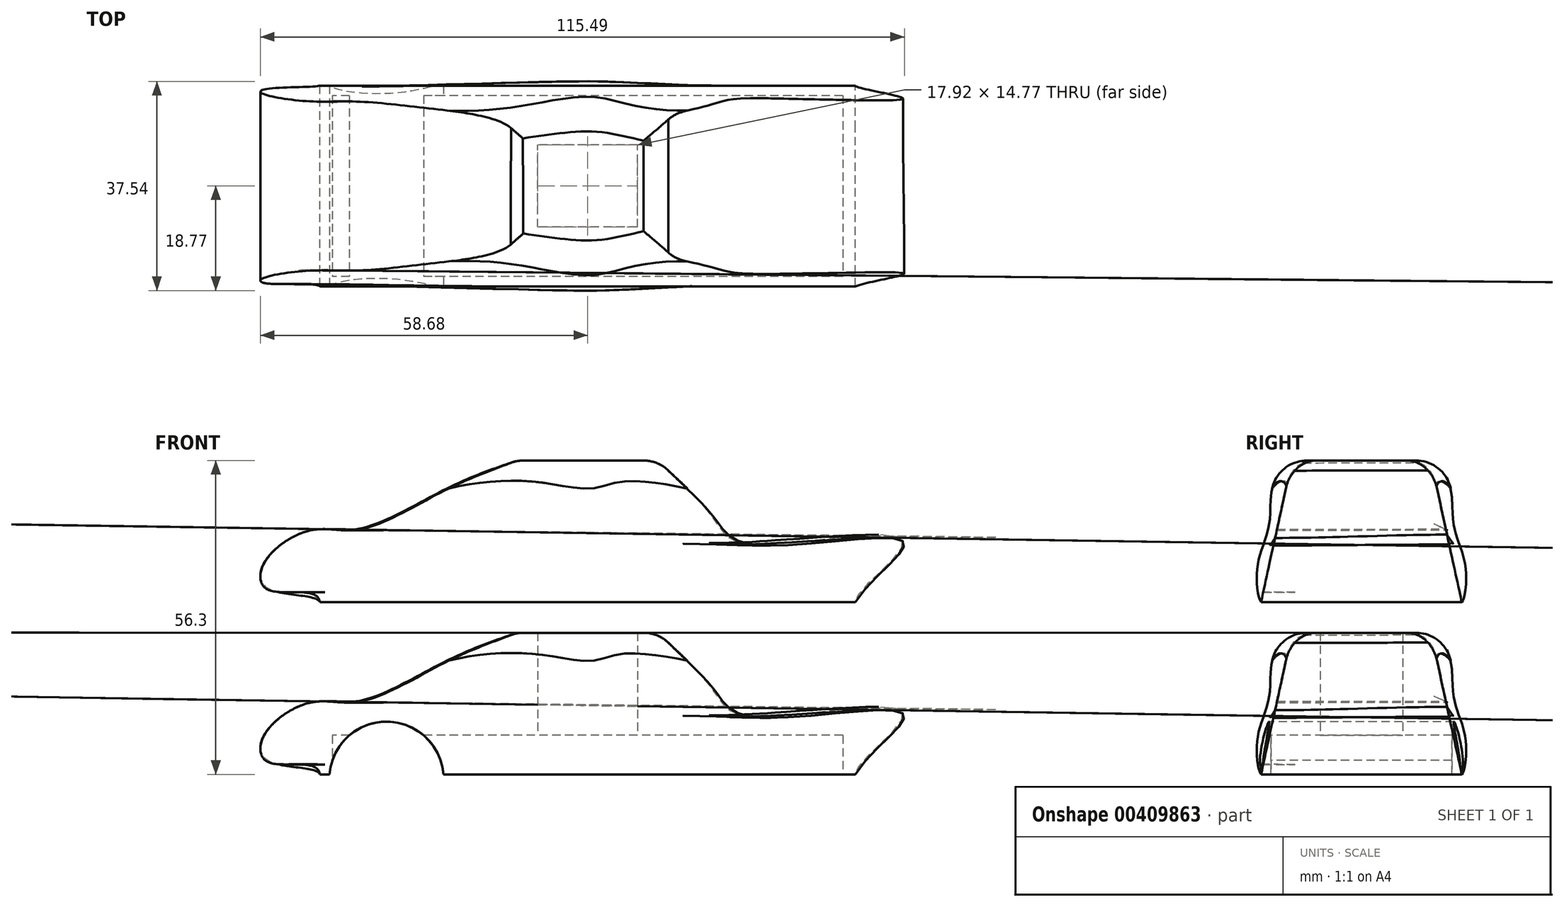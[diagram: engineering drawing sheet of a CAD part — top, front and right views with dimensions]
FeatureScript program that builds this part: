
annotation { "Feature Type Name" : "Feature", "Feature Type Description" : "" }
export const myFeature = defineFeature(function(context is Context, id is Id, definition is map)
    precondition{}
    {
        {
            var Q0;
            Q0=qCreatedBy(makeId("Top.planeOp"),FACE);
            var sketch = newSketch(context, id + "F0", { "sketchPlane" : qUnion([Q0])});
            skLineSegment(sketch, "E0.bottom", {"start": v(48, -18) * mm, "end": v(-48, -18) * mm});
            skLineSegment(sketch, "E0.top", {"start": v(48, 18) * mm, "end": v(-48, 18) * mm});
            skLineSegment(sketch, "E0.left", {"start": v(48, -18) * mm, "end": v(48, 18) * mm});
            skLineSegment(sketch, "E0.right", {"start": v(-48, -18) * mm, "end": v(-48, 18) * mm});
            skPoint(sketch, "E0.middle", {"position": v(0, 0) * mm});
            skLineSegment(sketch, "E1", {"start": v(0, 18) * mm, "end": v(0, -18) * mm, "construction": true});
            skSolve(sketch);
        }
        {
            var Q0;
            Q0=sQuery(id+"F0.wireOp",EDGE,"E0.bottom");
            cPoint(context, id + "F1", {"entities" : qUnion([Q0]), "parameter" : 0.5});
        }
        {
            var Q0;
            Q0=sQuery(id+"F0.wireOp",EDGE,"E1");
            var Q1;
            Q1 = qCreatedBy(id + "F1" ,VERTEX);
            cPlane(context, id + "F2", {"entities" : qUnion([Q0, Q1]), "cplaneType" : CPlaneType.LINE_POINT, "offset" : 25.4 * mm, "width" : 152.4 * mm, "height" : 152.4 * mm});
        }
        {
            var Q0;
            Q0=qCreatedBy(makeId("Top.planeOp"),FACE);
            cPlane(context, id + "F3", {"entities" : qUnion([Q0]), "cplaneType" : CPlaneType.OFFSET, "offset" : 25.4 * mm, "width" : 152.4 * mm, "height" : 152.4 * mm});
        }
        {
            var Q0;
            Q0=qCreatedBy(id+"F3.planeOp",FACE);
            var sketch = newSketch(context, id + "F4", { "sketchPlane" : qUnion([Q0])});
            skLineSegment(sketch, "E2.bottom", {"start": v(12.7, -12.45) * mm, "end": v(-12.7, -12.45) * mm});
            skLineSegment(sketch, "E2.top", {"start": v(12.7, 12.45) * mm, "end": v(-12.7, 12.45) * mm});
            skLineSegment(sketch, "E2.left", {"start": v(12.7, -12.45) * mm, "end": v(12.7, 12.45) * mm});
            skLineSegment(sketch, "E2.right", {"start": v(-12.7, -12.45) * mm, "end": v(-12.7, 12.45) * mm});
            skPoint(sketch, "E2.middle", {"position": v(0, 0) * mm});
            skLineSegment(sketch, "E3", {"start": v(0, 0) * mm, "end": v(0, -12.45) * mm, "construction": true});
            skLineSegment(sketch, "E4", {"start": v(-12.7, 0) * mm, "end": v(12.7, 0) * mm, "construction": true});
            skLineSegment(sketch, "E5", {"start": v(0, 0) * mm, "end": v(0, 12.45) * mm, "construction": true});
            skSolve(sketch);
        }
        {
            var Q0;
            Q0=sQuery(id+"F4.wireOp",VERTEX,"E3.end");
            var Q1;
            Q1=sQuery(id+"F0.wireOp",VERTEX,"E0.right.start");
            var Q2;
            Q2=sQuery(id+"F0.wireOp",VERTEX,"E0.bottom.start");
            cPlane(context, id + "F5", {"entities" : qUnion([Q0, Q1, Q2]), "cplaneType" : CPlaneType.THREE_POINT, "offset" : 25.4 * mm, "width" : 152.4 * mm, "height" : 152.4 * mm});
        }
        {
            var Q0;
            Q0=qCreatedBy(id+"F5.planeOp",FACE);
            var sketch = newSketch(context, id + "F6", { "sketchPlane" : qUnion([Q0])});
            skFitSpline(sketch, "E6", {"points": [v(12.7, 22.16) * mm, v(25.28, 16.84) * mm, v(40.86, 9.52) * mm, v(49.57, 9.36) * mm, v(58.12, 3.05) * mm, v(56.98, -1.7) * mm, v(48, -3.84) * mm], "startDerivative": vector(60.22, -24.2) * mm, "endDerivative": vector(-7.7, -56.28) * mm});
            skFitSpline(sketch, "E7", {"points": [v(-12.7, 22.16) * mm, v(-19.43, 15.4) * mm, v(-23.32, 10.85) * mm, v(-29.51, 6.74) * mm, v(-56.65, 7.22) * mm, v(-48, -3.84) * mm], "startDerivative": vector(-31.26, -33.19) * mm, "endDerivative": vector(39.78, -64.87) * mm});
            skSolve(sketch);
        }
        {
            var Q0;
            Q0=sQuery(id+"F4.wireOp",EDGE,"E2.top");
            cPoint(context, id + "F7", {"entities" : qUnion([Q0]), "parameter" : 0.5});
        }
        {
            var Q0;
            Q0 = qCreatedBy(id + "F7" ,VERTEX);
            var Q1;
            Q1=sQuery(id+"F0.wireOp",VERTEX,"E0.left.end");
            var Q2;
            Q2=sQuery(id+"F0.wireOp",VERTEX,"E0.right.end");
            cPlane(context, id + "F8", {"entities" : qUnion([Q0, Q1, Q2]), "cplaneType" : CPlaneType.THREE_POINT, "offset" : 25.4 * mm, "width" : 152.4 * mm, "height" : 152.4 * mm});
        }
        {
            var Q0;
            Q0=qCreatedBy(id+"F8.planeOp",FACE);
            var sketch = newSketch(context, id + "F9", { "sketchPlane" : qUnion([Q0])});
            skFitSpline(sketch, "E8", {"points": [v(12.7, 22.16) * mm, v(19.29, 15.59) * mm, v(23.6, 10) * mm, v(29.61, 6.76) * mm, v(56.55, 7.19) * mm, v(48, -3.84) * mm], "startDerivative": vector(33.12, -36.07) * mm, "endDerivative": vector(5.37, -27.82) * mm});
            skFitSpline(sketch, "E9", {"points": [v(-12.45, 22.25) * mm, v(-24.96, 17.16) * mm, v(-41.15, 9.6) * mm, v(-49.8, 9.32) * mm, v(-58.17, 3.06) * mm, v(-56.92, -1.5) * mm, v(-48, -3.84) * mm], "startDerivative": vector(-64.64, -23.54) * mm, "endDerivative": vector(9.88, -27.36) * mm});
            skSolve(sketch);
        }
        {
            var Q0;
            Q0=sQuery(id+"F0.wireOp",EDGE,"E0.bottom");
            cPlane(context, id + "F10", {"entities" : qUnion([Q0]), "cplaneType" : CPlaneType.MID_PLANE, "offset" : 25.4 * mm, "width" : 152.4 * mm, "height" : 152.4 * mm});
        }
        {
            var Q0;
            Q0=qCreatedBy(id+"F10.planeOp",FACE);
            var sketch = newSketch(context, id + "F11", { "sketchPlane" : qUnion([Q0])});
            skFitSpline(sketch, "E10", {"points": [v(12.45, 25.4) * mm, v(16.46, 14.53) * mm, v(18.6, 6.63) * mm, v(18, 0) * mm], "startDerivative": vector(36.42, -22.65) * mm, "endDerivative": vector(-6.58, -9) * mm});
            skLineSegment(sketch, "E11", {"start": v(0, 25.4) * mm, "end": v(0, 0) * mm, "construction": true});
            skFitSpline(sketch, "E12.MirrorCS", {"points": [v(-12.45, 25.4) * mm, v(-16.46, 14.53) * mm, v(-18.6, 6.63) * mm, v(-18, 0) * mm], "startDerivative": vector(-36.42, -22.65) * mm, "endDerivative": vector(6.58, -9) * mm});
            skSolve(sketch);
        }
        {
            var Q0;
            Q0=makeQuery(id+"F0.imprint","IMPRINT",FACE,{"disambiguationData":[TD([[makeQuery(id+"F0.imprint","IMPRINT",EDGE,{"derivedFrom":sQuery(id+"F0.wireOp",EDGE,"E0.bottom")}),-1.0]])]});
            var Q1;
            Q1=makeQuery(id+"F4.imprint","IMPRINT",FACE,{"disambiguationData":[TD([[makeQuery(id+"F4.imprint","IMPRINT",EDGE,{"derivedFrom":sQuery(id+"F4.wireOp",EDGE,"E2.bottom")}),-1.0]])]});
            var Q2;
            Q2=sQuery(id+"F9.wireOp",EDGE,"E9");
            var Q3;
            Q3=sQuery(id+"F6.wireOp",EDGE,"E6");
            var Q4;
            Q4=sQuery(id+"F6.wireOp",EDGE,"E7");
            var Q5;
            Q5=sQuery(id+"F9.wireOp",EDGE,"E8");
            var Q6;
            Q6=sQuery(id+"F11.wireOp",EDGE,"E12.MirrorCS");
            var Q7;
            Q7=sQuery(id+"F11.wireOp",EDGE,"E10");
            loft(context, id + "F12", {"addGuides" : true, "sheetProfilesArray" : [{ "sheetProfileEntities" : qUnion([Q0]) }, { "sheetProfileEntities" : qUnion([Q1]) }], "guidesArray" : [{ "guideEntities" : qUnion([Q2]), "guideDerivativeType" : LoftGuideDerivativeType.DEFAULT, "guideDerivativeMagnitude" : 1 }, { "guideEntities" : qUnion([Q3]), "guideDerivativeType" : LoftGuideDerivativeType.DEFAULT, "guideDerivativeMagnitude" : 1 }, { "guideEntities" : qUnion([Q4]), "guideDerivativeType" : LoftGuideDerivativeType.DEFAULT, "guideDerivativeMagnitude" : 1 }, { "guideEntities" : qUnion([Q5]), "guideDerivativeType" : LoftGuideDerivativeType.DEFAULT, "guideDerivativeMagnitude" : 1 }, { "guideEntities" : qUnion([Q6]), "guideDerivativeType" : LoftGuideDerivativeType.DEFAULT, "guideDerivativeMagnitude" : 1 }, { "guideEntities" : qUnion([Q7]), "guideDerivativeType" : LoftGuideDerivativeType.DEFAULT, "guideDerivativeMagnitude" : 1 }]});
        }
        {
            var Q0;
            Q0=makeQuery(id+"F12.opLoft","MID_CAP_EDGE",EDGE,{"disambiguationData":[OSD([sQuery(id+"F4.wireOp",EDGE,"E2.right"),sQuery(id+"F6.wireOp",EDGE,"E6"),sQuery(id+"F9.wireOp",EDGE,"E9")])],"capPos":1.0});
            var Q1;
            Q1=makeQuery(id+"F12.opLoft","MID_CAP_EDGE",EDGE,{"disambiguationData":[OSD([sQuery(id+"F4.wireOp",EDGE,"E2.bottom"),sQuery(id+"F6.wireOp",EDGE,"E6"),sQuery(id+"F11.wireOp",EDGE,"E10")])],"capPos":1.0});
            var Q2;
            Q2=makeQuery(id+"F12.opLoft","MID_CAP_EDGE",EDGE,{"disambiguationData":[OSD([sQuery(id+"F4.wireOp",EDGE,"E2.top"),sQuery(id+"F9.wireOp",EDGE,"E8"),sQuery(id+"F11.wireOp",EDGE,"E12.MirrorCS")])],"capPos":1.0});
            var Q3;
            Q3=makeQuery(id+"F12.opLoft","MID_CAP_EDGE",EDGE,{"disambiguationData":[OSD([sQuery(id+"F4.wireOp",EDGE,"E2.left"),sQuery(id+"F6.wireOp",EDGE,"E7"),sQuery(id+"F9.wireOp",EDGE,"E8")])],"capPos":1.0});
            fillet(context, id + "F13", {"entities" : qUnion([Q0, Q1, Q2, Q3]), "radius" : 6.35 * mm, "allowEdgeOverflow" : false});
        }
        {
            var Q0;
            Q0=makeQuery(id+"F12.opLoft","SWEPT_BODY",BODY,{"disambiguationData":[OSD([makeQuery(id+"F0.imprint","IMPRINT",FACE,{"disambiguationData":[TD([[makeQuery(id+"F0.imprint","IMPRINT",EDGE,{"derivedFrom":sQuery(id+"F0.wireOp",EDGE,"E0.bottom")}),-1.0]])]}),makeQuery(id+"F4.imprint","IMPRINT",FACE,{"disambiguationData":[TD([[makeQuery(id+"F4.imprint","IMPRINT",EDGE,{"derivedFrom":sQuery(id+"F4.wireOp",EDGE,"E2.bottom")}),-1.0]])]}),sQuery(id+"F6.wireOp",EDGE,"E6"),sQuery(id+"F6.wireOp",EDGE,"E7"),sQuery(id+"F9.wireOp",EDGE,"E8"),sQuery(id+"F9.wireOp",EDGE,"E9"),sQuery(id+"F11.wireOp",EDGE,"E10"),sQuery(id+"F11.wireOp",EDGE,"E12.MirrorCS")])]});
            transform(context, id + "F14", {"entities" : qUnion([Q0]), "transformType" : TransformType.TRANSLATION_3D, "dx" : 0 * mm, "dy" : 0 * mm, "dz" : -30.9 * mm, "makeCopy" : true});
        }
        {
            var Q0;
            Q0=makeQuery(id+"F14.opPattern","COPY",FACE,{"derivedFrom":makeQuery(id+"F12.opLoft","CAP_FACE",FACE,{"disambiguationData":[OSD([makeQuery(id+"F0.imprint","IMPRINT",FACE,{"disambiguationData":[TD([[makeQuery(id+"F0.imprint","IMPRINT",EDGE,{"derivedFrom":sQuery(id+"F0.wireOp",EDGE,"E0.bottom")}),-1.0]])]})])],"isStart":true}),"instanceName":"1"});
            var sketch = newSketch(context, id + "F15", { "sketchPlane" : qUnion([Q0])});
            skLineSegment(sketch, "E13.bottom", {"start": v(45.76, -16.22) * mm, "end": v(-45.76, -16.22) * mm});
            skLineSegment(sketch, "E13.top", {"start": v(45.76, 16.22) * mm, "end": v(-45.76, 16.22) * mm});
            skLineSegment(sketch, "E13.left", {"start": v(45.76, -16.22) * mm, "end": v(45.76, 16.22) * mm});
            skLineSegment(sketch, "E13.right", {"start": v(-45.76, -16.22) * mm, "end": v(-45.76, 16.22) * mm});
            skPoint(sketch, "E13.middle", {"position": v(0, 0) * mm});
            skLineSegment(sketch, "E14.bottom", {"start": v(8.96, 7.39) * mm, "end": v(-8.96, 7.39) * mm});
            skLineSegment(sketch, "E14.top", {"start": v(8.96, -7.39) * mm, "end": v(-8.96, -7.39) * mm});
            skLineSegment(sketch, "E14.left", {"start": v(8.96, 7.39) * mm, "end": v(8.96, -7.39) * mm});
            skLineSegment(sketch, "E14.right", {"start": v(-8.96, 7.39) * mm, "end": v(-8.96, -7.39) * mm});
            skSolve(sketch);
        }
        {
            var Q0;
            Q0=makeQuery(id+"F15.imprint","IMPRINT",FACE,{"disambiguationData":[TD([[makeQuery(id+"F15.imprint","IMPRINT",EDGE,{"derivedFrom":sQuery(id+"F15.wireOp",EDGE,"E13.bottom")}),-1.0]])]});
            extrude(context, id + "F16", {"entities" : qUnion([Q0]), "operationType" : NewBodyOperationType.REMOVE, "oppositeDirection" : true, "depth" : 7 * mm});
        }
        {
            var Q0;
            Q0=makeQuery(id+"F16.boolean.opBoolean","SPLIT",FACE,{"disambiguationData":[TD([makeQuery(id+"F16.opExtrude","SWEPT_FACE",FACE,{"disambiguationData":[OSD([sQuery(id+"F15.wireOp",EDGE,"E14.bottom")])]})])],"derivedFrom":makeQuery(id+"F14.opPattern","COPY",FACE,{"derivedFrom":makeQuery(id+"F12.opLoft","CAP_FACE",FACE,{"disambiguationData":[OSD([makeQuery(id+"F0.imprint","IMPRINT",FACE,{"disambiguationData":[TD([[makeQuery(id+"F0.imprint","IMPRINT",EDGE,{"derivedFrom":sQuery(id+"F0.wireOp",EDGE,"E0.bottom")}),-1.0]])]})])],"isStart":true}),"instanceName":"1"})});
            extrude(context, id + "F17", {"entities" : qUnion([Q0]), "operationType" : NewBodyOperationType.REMOVE, "oppositeDirection" : true, "depth" : 29.5 * mm});
        }
        {
            var Q0;
            Q0=qCreatedBy(id+"F2.planeOp",FACE);
            var sketch = newSketch(context, id + "F18", { "sketchPlane" : qUnion([Q0])});
            skCircle(sketch, "E15", {"center": v(-36.06, -31.7) * mm, "radius": 10.25 * mm});
            skLineSegment(sketch, "E16", {"start": v(0, 0) * mm, "end": v(0, -50.87) * mm, "construction": true});
            skCircle(sketch, "E17.MirrorC", {"center": v(34.09, -31.85) * mm, "radius": 10.25 * mm});
            skSolve(sketch);
        }
        {
            var Q0;
            Q0=makeQuery(id+"F18.imprint","IMPRINT",FACE,{"disambiguationData":[TD([[makeQuery(id+"F18.imprint","IMPRINT",EDGE,{"derivedFrom":sQuery(id+"F18.wireOp",EDGE,"E17.MirrorC")}),-1.0]])]});
            var Q1;
            Q1=makeQuery(id+"F18.imprint","IMPRINT",FACE,{"disambiguationData":[TD([[makeQuery(id+"F18.imprint","IMPRINT",EDGE,{"derivedFrom":sQuery(id+"F18.wireOp",EDGE,"E15")}),1.0]])]});
            extrude(context, id + "F19", {"entities" : qUnion([Q0, Q1]), "operationType" : NewBodyOperationType.REMOVE, "oppositeDirection" : true, "depth" : 44.2 * mm});
        }
        {
            var Q0;
            Q0=makeQuery(id+"F18.imprint","IMPRINT",FACE,{"disambiguationData":[TD([[makeQuery(id+"F18.imprint","IMPRINT",EDGE,{"derivedFrom":sQuery(id+"F18.wireOp",EDGE,"E15")}),1.0]])]});
            extrude(context, id + "F20", {"entities" : qUnion([Q0]), "operationType" : NewBodyOperationType.REMOVE, "depth" : 34.9 * mm});
        }
    });
